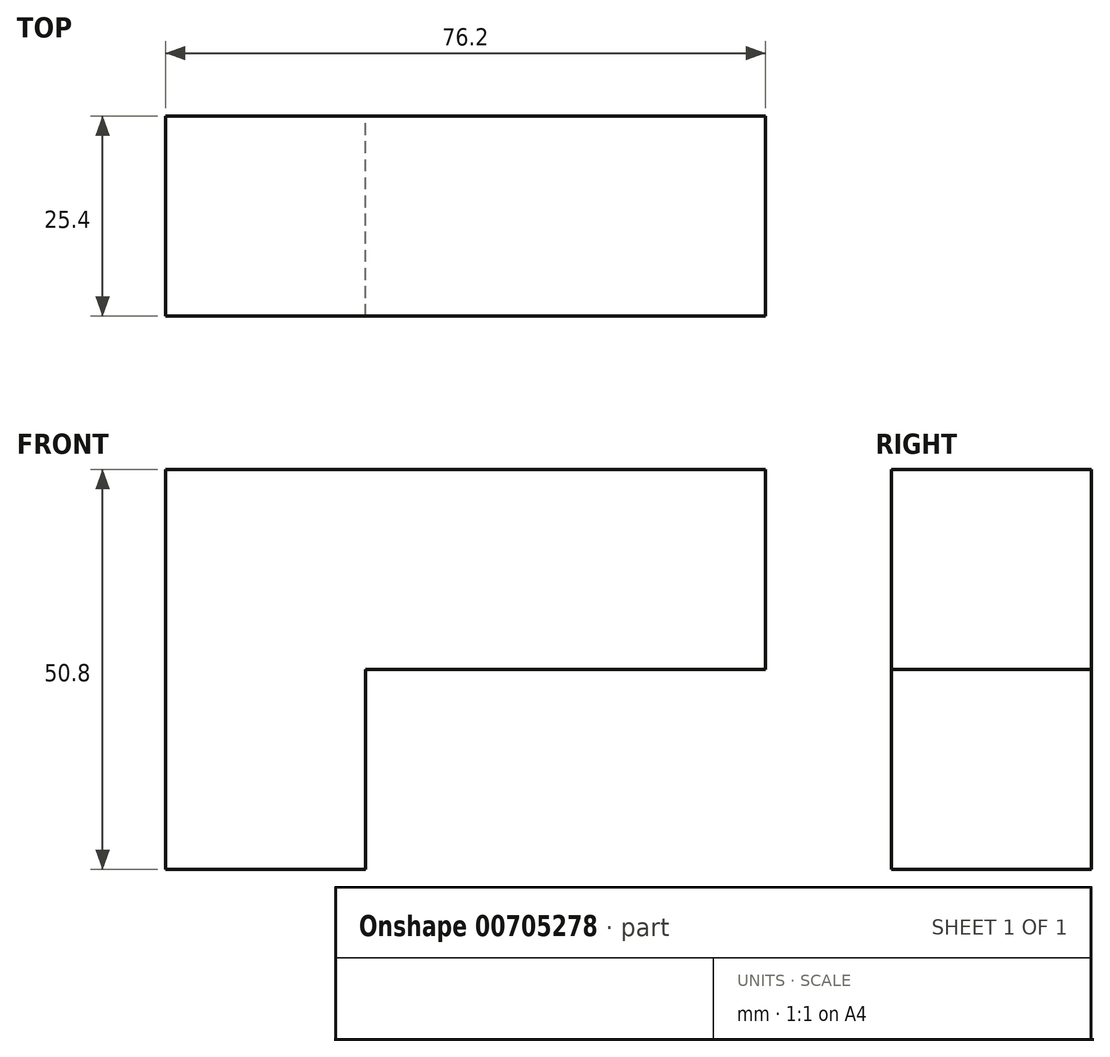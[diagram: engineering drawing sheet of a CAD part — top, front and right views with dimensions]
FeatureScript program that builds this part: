
annotation { "Feature Type Name" : "Feature", "Feature Type Description" : "" }
export const myFeature = defineFeature(function(context is Context, id is Id, definition is map)
    precondition{}
    {
        {
            var Q0;
            Q0=qCreatedBy(makeId("Front.planeOp"),FACE);
            var sketch = newSketch(context, id + "F0", { "sketchPlane" : qUnion([Q0])});
            skLineSegment(sketch, "E0.bottom", {"start": v(0, 0) * mm, "end": v(-25.4, 0) * mm});
            skLineSegment(sketch, "E0.top", {"start": v(0, -25.4) * mm, "end": v(-25.4, -25.4) * mm});
            skLineSegment(sketch, "E0.left", {"start": v(0, 0) * mm, "end": v(0, -25.4) * mm});
            skLineSegment(sketch, "E0.right", {"start": v(-25.4, 0) * mm, "end": v(-25.4, -25.4) * mm});
            skLineSegment(sketch, "E1.top", {"start": v(0, 25.4) * mm, "end": v(-25.4, 25.4) * mm});
            skLineSegment(sketch, "E1.left", {"start": v(0, 0) * mm, "end": v(0, 25.4) * mm});
            skLineSegment(sketch, "E1.right", {"start": v(-25.4, 0) * mm, "end": v(-25.4, 25.4) * mm});
            skLineSegment(sketch, "E2.bottom", {"start": v(0, 25.4) * mm, "end": v(25.4, 25.4) * mm});
            skLineSegment(sketch, "E2.top", {"start": v(0, 0) * mm, "end": v(25.4, 0) * mm});
            skLineSegment(sketch, "E2.left", {"start": v(0, 25.4) * mm, "end": v(0, 0) * mm});
            skLineSegment(sketch, "E2.right", {"start": v(25.4, 25.4) * mm, "end": v(25.4, 0) * mm});
            skLineSegment(sketch, "E3.bottom", {"start": v(25.4, 25.4) * mm, "end": v(50.8, 25.4) * mm});
            skLineSegment(sketch, "E3.top", {"start": v(25.4, 0) * mm, "end": v(50.8, 0) * mm});
            skLineSegment(sketch, "E3.right", {"start": v(50.8, 25.4) * mm, "end": v(50.8, 0) * mm});
            skLineSegment(sketch, "E4.bottom", {"start": v(50.8, 0) * mm, "end": v(25.4, 0) * mm});
            skLineSegment(sketch, "E4.top", {"start": v(50.8, -25.4) * mm, "end": v(25.4, -25.4) * mm});
            skLineSegment(sketch, "E4.left", {"start": v(50.8, 0) * mm, "end": v(50.8, -25.4) * mm});
            skLineSegment(sketch, "E4.right", {"start": v(25.4, 0) * mm, "end": v(25.4, -25.4) * mm});
            skSolve(sketch);
        }
        {
            var Q0;
            Q0=makeQuery(id+"F0.imprint","IMPRINT",FACE,{"disambiguationData":[TD([[makeQuery(id+"F0.imprint","IMPRINT",EDGE,{"derivedFrom":sQuery(id+"F0.wireOp",EDGE,"E0.bottom")}),-1.0]])]});
            var Q1;
            Q1=makeQuery(id+"F0.imprint","IMPRINT",FACE,{"disambiguationData":[TD([[makeQuery(id+"F0.imprint","IMPRINT",EDGE,{"derivedFrom":sQuery(id+"F0.wireOp",EDGE,"E2.bottom")}),-1.0]])]});
            var Q2;
            Q2=makeQuery(id+"F0.imprint","IMPRINT",FACE,{"disambiguationData":[TD([[makeQuery(id+"F0.imprint","IMPRINT",EDGE,{"derivedFrom":sQuery(id+"F0.wireOp",EDGE,"E3.bottom")}),-1.0]])]});
            var Q3;
            Q3=makeQuery(id+"F0.imprint","IMPRINT",FACE,{"disambiguationData":[TD([[makeQuery(id+"F0.imprint","IMPRINT",EDGE,{"derivedFrom":sQuery(id+"F0.wireOp",EDGE,"E4.bottom")}),1.0]])]});
            var Q4;
            Q4=makeQuery(id+"F0.imprint","IMPRINT",FACE,{"disambiguationData":[TD([[makeQuery(id+"F0.imprint","IMPRINT",EDGE,{"derivedFrom":sQuery(id+"F0.wireOp",EDGE,"E0.top")}),-1.0]])]});
            extrude(context, id + "F1", {"entities" : qUnion([Q0, Q1, Q2, Q3, Q4]), "depth" : 25.4 * mm, "offsetDistance" : 25.4 * mm});
        }
    });
